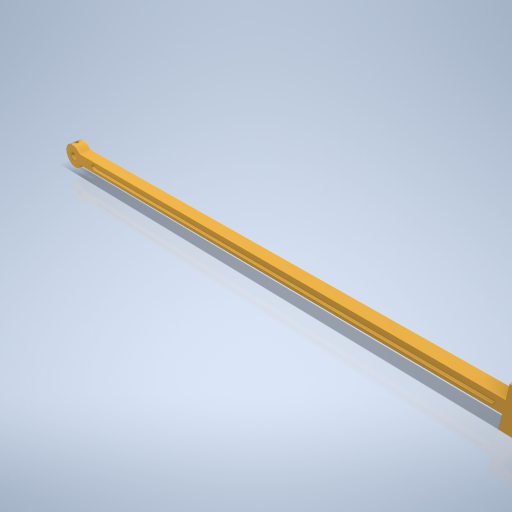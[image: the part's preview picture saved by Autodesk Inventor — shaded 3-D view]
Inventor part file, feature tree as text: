
AUTODESK INVENTOR PART (.ipt)
format: ipt  version: 2024.2 (Build 282272000, 272)  size: 348,160 bytes
history: native  units: mm
features: sketch x6, extrude x5, hole x3, plane x2, projected_geometry x2, fillet x1
ambient origin geometry x8: Origin, YZ Plane, XZ Plane, XY Plane, X Axis, Y Axis, Z Axis, Center Point
bodies: Volumenkörper1 (feature_tree)
feature tree (19):
  sketch  "Skizze1"  dims[d0=39.0mm d1=30.0mm]
  extrude  "Extrusion1"  Depth=30.0mm
  extrude  "Extrusion2"  Depth=12.0mm
  extrude  "Extrusion3"  Depth=6.0mm
  hole  "Bohrung1"  [1 undecoded]
  plane  "Arbeitsebene1"
  extrude  "Extrusion4"  Depth=3.0mm TaperAngle=0.0deg
  extrude  "Extrusion5"  TaperAngle=0.0deg  [1 undecoded]
  fillet  "Rundung1"  Radius=24.0mm
  plane  "Arbeitsebene2"
  hole  "Bohrung2"  [1 undecoded]
  hole  "Bohrung3"  [1 undecoded]
  sketch  "Skizze2"  dims[d2=470.0mm d3=12.0mm]
  sketch  "Skizze4"  dims[d4=6.0mm d5=6.0mm]
  sketch  "Skizze5"  dims[d6=3.0mm d8=12.0mm d9=0.0mm]
  sketch  "Skizze6"  dims[d10=3.0mm d11=0.0mm d12=3.0mm d13=0.0mm]
  projected_geometry  "Projizierte Kontur1"
  sketch  "Skizze7"  dims[d14=18.0mm d15=6.0mm d16=4.0mm d17=2.0mm d18=90.0deg d19=8.0mm d20=20.594885mm d23=0.0mm d24=24.0mm d25=12.0mm d26=0.0mm d27=420.0mm d28=7.5mm d29=12.0mm d30=0.0mm d31=3.0mm d32=12.0mm d34=4.5mm d35=6.0mm d36=4.0mm d37=2.0mm d38=90.0deg d39=8.0mm d40=20.594885mm d41=6.0mm d42=6.0mm d43=4.0mm d44=2.0mm d45=90.0deg d46=8.0mm d47=20.594885mm d48=6.0mm d50=13.5mm d51=13.5mm d33=0.5mm]
  projected_geometry  "Projizierte Kontur2"
note: 4 required parameter values undecoded (feature->parameter linkage not recoverable at this tier; creation-order binding heuristic only, values carry confidence <= 0.55)
